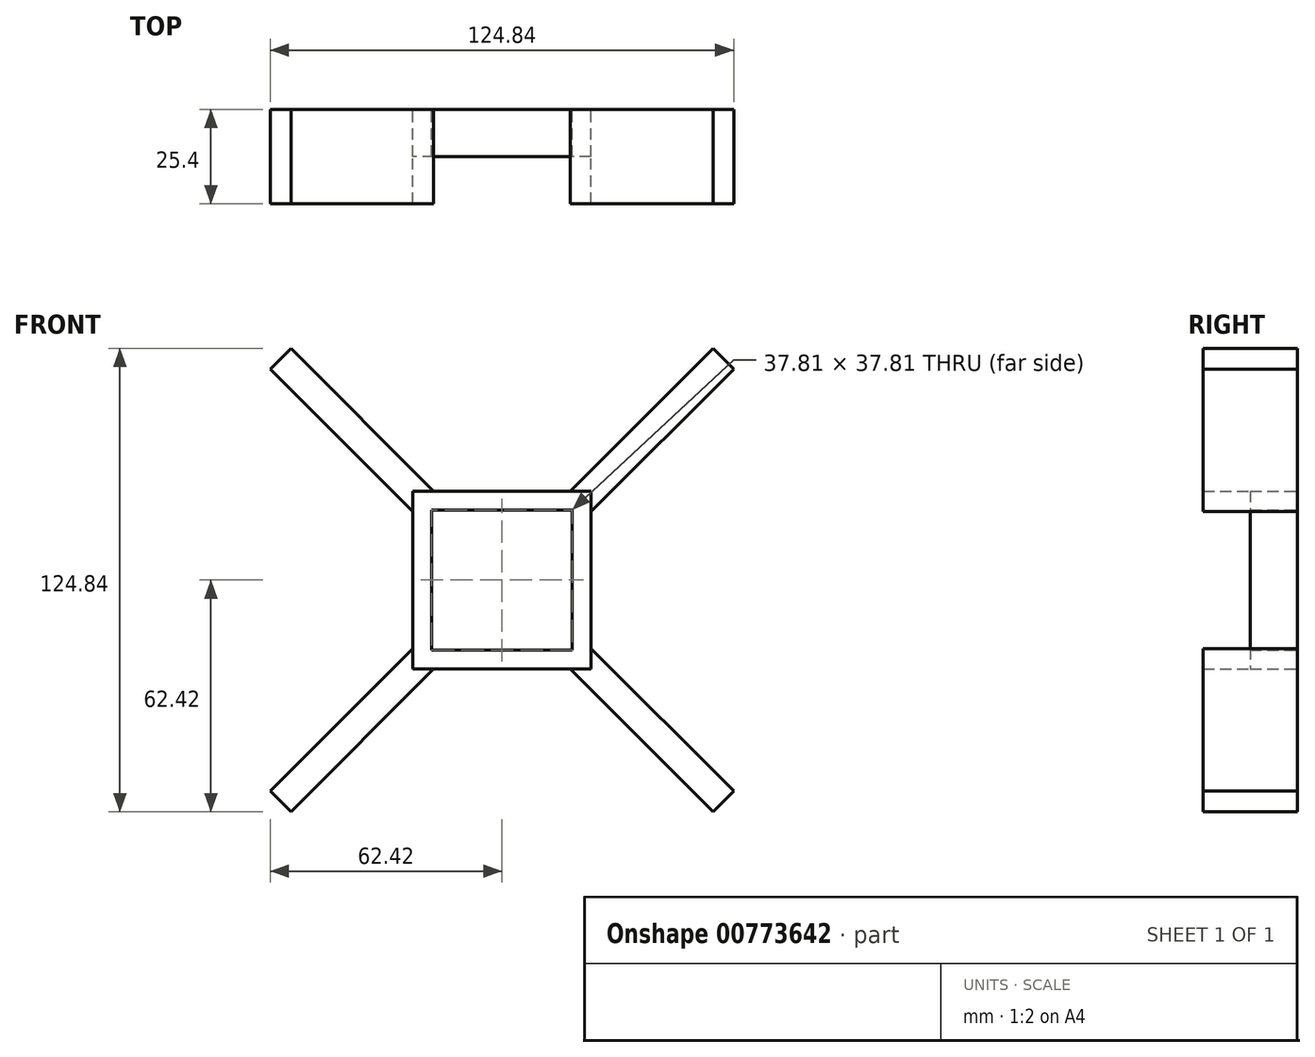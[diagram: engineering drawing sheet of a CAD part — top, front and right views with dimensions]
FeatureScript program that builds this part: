
annotation { "Feature Type Name" : "Feature", "Feature Type Description" : "" }
export const myFeature = defineFeature(function(context is Context, id is Id, definition is map)
    precondition{}
    {
        {
            var Q0;
            Q0=qCreatedBy(makeId("Front.planeOp"),FACE);
            var sketch = newSketch(context, id + "F0", { "sketchPlane" : qUnion([Q0])});
            skLineSegment(sketch, "E0.bottom", {"start": v(23.98, 23.98) * mm, "end": v(-23.98, 23.98) * mm});
            skLineSegment(sketch, "E0.top", {"start": v(23.98, -23.98) * mm, "end": v(-23.98, -23.98) * mm});
            skLineSegment(sketch, "E0.left", {"start": v(23.98, 23.98) * mm, "end": v(23.98, -23.98) * mm});
            skLineSegment(sketch, "E0.right", {"start": v(-23.98, 23.98) * mm, "end": v(-23.98, -23.98) * mm});
            skPoint(sketch, "E0.middle", {"position": v(0, 0) * mm});
            skLineSegment(sketch, "E1.bottom", {"start": v(18.9, 18.9) * mm, "end": v(-18.9, 18.9) * mm});
            skLineSegment(sketch, "E1.top", {"start": v(18.9, -18.9) * mm, "end": v(-18.9, -18.9) * mm});
            skLineSegment(sketch, "E1.left", {"start": v(18.9, 18.9) * mm, "end": v(18.9, -18.9) * mm});
            skLineSegment(sketch, "E1.right", {"start": v(-18.9, 18.9) * mm, "end": v(-18.9, -18.9) * mm});
            skLineSegment(sketch, "E2", {"start": v(23.98, 23.98) * mm, "end": v(-23.98, -23.98) * mm, "construction": true});
            skLineSegment(sketch, "E3", {"start": v(56.86, 62.42) * mm, "end": v(18.42, 23.98) * mm});
            skLineSegment(sketch, "E4.MirrorCS", {"start": v(62.42, 56.86) * mm, "end": v(23.98, 18.42) * mm});
            skLineSegment(sketch, "E5", {"start": v(-62.42, -56.86) * mm, "end": v(-56.86, -62.42) * mm});
            skLineSegment(sketch, "E6", {"start": v(56.86, 62.42) * mm, "end": v(62.42, 56.86) * mm});
            skLineSegment(sketch, "E7.trimOffspring", {"start": v(-23.98, -18.42) * mm, "end": v(-62.42, -56.86) * mm});
            skLineSegment(sketch, "E8.trimOffspring", {"start": v(-18.42, -23.98) * mm, "end": v(-56.86, -62.42) * mm});
            skLineSegment(sketch, "E9", {"start": v(0, 23.98) * mm, "end": v(0, -23.98) * mm, "construction": true});
            skLineSegment(sketch, "E10.MirrorCS", {"start": v(-56.86, 62.42) * mm, "end": v(-18.42, 23.98) * mm});
            skLineSegment(sketch, "E11.MirrorCS", {"start": v(-62.42, 56.86) * mm, "end": v(-23.98, 18.42) * mm});
            skLineSegment(sketch, "E12.MirrorCS", {"start": v(18.42, -23.98) * mm, "end": v(56.86, -62.42) * mm});
            skLineSegment(sketch, "E13.MirrorCS", {"start": v(23.98, -18.42) * mm, "end": v(62.42, -56.86) * mm});
            skLineSegment(sketch, "E14.MirrorCS", {"start": v(62.42, -56.86) * mm, "end": v(56.86, -62.42) * mm});
            skLineSegment(sketch, "E15.MirrorCS", {"start": v(-56.86, 62.42) * mm, "end": v(-62.42, 56.86) * mm});
            skCircle(sketch, "E16", {"center": v(-59.64, -59.64) * mm, "radius": 18.48 * mm});
            skLineSegment(sketch, "E17", {"start": v(-23.98, 23.98) * mm, "end": v(23.98, -23.98) * mm, "construction": true});
            skCircle(sketch, "E18.MirrorC", {"center": v(59.64, 59.64) * mm, "radius": 18.48 * mm});
            skCircle(sketch, "E19.MirrorC", {"center": v(-59.64, 59.64) * mm, "radius": 18.48 * mm});
            skCircle(sketch, "E20.MirrorC", {"center": v(59.64, -59.64) * mm, "radius": 18.48 * mm});
            skSolve(sketch);
        }
        {
            var Q0;
            Q0=makeQuery(id+"F0.imprint","IMPRINT",FACE,{"disambiguationData":[TD([[makeQuery(id+"F0.imprint","IMPRINT",EDGE,{"derivedFrom":sQuery(id+"F0.wireOp",EDGE,"E0.bottom")}),1.0]])]});
            extrude(context, id + "F1", {"entities" : qUnion([Q0]), "flatOperationType" : FlatOperationType.REMOVE, "depth" : 12.7 * mm, "offsetDistance" : 25.4 * mm, "domain" : OperationDomain.MODEL});
        }
        {
            var Q0;
            Q0=sQuery(id+"F0.wireOp",EDGE,"E19.MirrorC");
            extrude(context, id + "F2", {"bodyType" : ToolBodyType.SURFACE, "surfaceEntities" : qUnion([Q0]), "depth" : 50.8 * mm, "offsetDistance" : 25.4 * mm});
        }
        {
            var Q0;
            Q0=sQuery(id+"F0.wireOp",EDGE,"E16");
            var Q1;
            Q1=sQuery(id+"F0.wireOp",EDGE,"E20.MirrorC");
            var Q2;
            Q2=sQuery(id+"F0.wireOp",EDGE,"E18.MirrorC");
            extrude(context, id + "F3", {"bodyType" : ToolBodyType.SURFACE, "surfaceEntities" : qUnion([Q0, Q1, Q2]), "depth" : 50.8 * mm, "offsetDistance" : 25.4 * mm});
        }
        {
            var Q0;
            {var subQ1=sQuery(id+"F0.wireOp",EDGE,"E0.right");var subQ7=sQuery(id+"F0.wireOp",EDGE,"E0.bottom");var subQ8=makeQuery(id+"F0.imprint","INTERSECT",VERTEX,{"derivedFrom":[subQ7,subQ1]});Q0=makeQuery(id+"F0.imprint","IMPRINT",FACE,{"disambiguationData":[TD([[makeQuery(id+"F0.imprint","IMPRINT",EDGE,{"disambiguationData":[TD([[subQ8,1.0]])],"derivedFrom":subQ7}),-1.0]])]});}
            var Q1;
            {var subQ0=sQuery(id+"F0.wireOp",EDGE,"E15.MirrorCS");Q1=makeQuery(id+"F0.imprint","IMPRINT",FACE,{"disambiguationData":[TD([[makeQuery(id+"F0.imprint","IMPRINT",EDGE,{"derivedFrom":subQ0}),1.0]])]});}
            var Q2;
            {var subQ0=sQuery(id+"F0.wireOp",EDGE,"E5");Q2=makeQuery(id+"F0.imprint","IMPRINT",FACE,{"disambiguationData":[TD([[makeQuery(id+"F0.imprint","IMPRINT",EDGE,{"derivedFrom":subQ0}),1.0]])]});}
            var Q3;
            {var subQ1=sQuery(id+"F0.wireOp",EDGE,"E0.top");var subQ6=sQuery(id+"F0.wireOp",EDGE,"E0.right");var subQ9=makeQuery(id+"F0.imprint","INTERSECT",VERTEX,{"derivedFrom":[subQ1,subQ6]});Q3=makeQuery(id+"F0.imprint","IMPRINT",FACE,{"disambiguationData":[TD([[makeQuery(id+"F0.imprint","IMPRINT",EDGE,{"disambiguationData":[TD([[subQ9,1.0]])],"derivedFrom":subQ1}),1.0]])]});}
            var Q4;
            {var subQ1=sQuery(id+"F0.wireOp",EDGE,"E0.left");var subQ6=sQuery(id+"F0.wireOp",EDGE,"E0.top");var subQ9=makeQuery(id+"F0.imprint","INTERSECT",VERTEX,{"derivedFrom":[subQ6,subQ1]});Q4=makeQuery(id+"F0.imprint","IMPRINT",FACE,{"disambiguationData":[TD([[makeQuery(id+"F0.imprint","IMPRINT",EDGE,{"disambiguationData":[TD([[subQ9,-1.0]])],"derivedFrom":subQ6}),1.0]])]});}
            var Q5;
            {var subQ0=sQuery(id+"F0.wireOp",EDGE,"E14.MirrorCS");Q5=makeQuery(id+"F0.imprint","IMPRINT",FACE,{"disambiguationData":[TD([[makeQuery(id+"F0.imprint","IMPRINT",EDGE,{"derivedFrom":subQ0}),-1.0]])]});}
            var Q6;
            {var subQ0=sQuery(id+"F0.wireOp",EDGE,"E6");Q6=makeQuery(id+"F0.imprint","IMPRINT",FACE,{"disambiguationData":[TD([[makeQuery(id+"F0.imprint","IMPRINT",EDGE,{"derivedFrom":subQ0}),-1.0]])]});}
            var Q7;
            {var subQ1=sQuery(id+"F0.wireOp",EDGE,"E0.left");var subQ6=sQuery(id+"F0.wireOp",EDGE,"E0.bottom");var subQ9=makeQuery(id+"F0.imprint","INTERSECT",VERTEX,{"derivedFrom":[subQ6,subQ1]});Q7=makeQuery(id+"F0.imprint","IMPRINT",FACE,{"disambiguationData":[TD([[makeQuery(id+"F0.imprint","IMPRINT",EDGE,{"disambiguationData":[TD([[subQ9,-1.0]])],"derivedFrom":subQ6}),-1.0]])]});}
            extrude(context, id + "F4", {"entities" : qUnion([Q0, Q1, Q2, Q3, Q4, Q5, Q6, Q7]), "operationType" : NewBodyOperationType.ADD, "depth" : 25.4 * mm, "offsetDistance" : 25.4 * mm});
        }
    });
